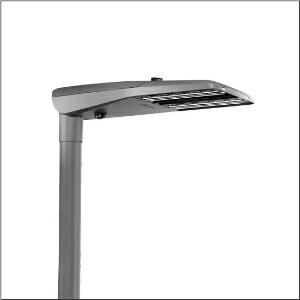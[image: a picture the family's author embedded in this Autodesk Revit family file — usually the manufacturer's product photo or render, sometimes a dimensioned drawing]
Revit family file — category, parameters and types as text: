
# Revit family: streetlight_sl_11_iq_midi___st0_5st0_5_5xc3h51y08me_12eb
name_source: partatom
category: Lighting Fixtures
units: mm (PartAtom-declared; Revit-internal decimal feet)

## family parameters
Cut with Voids When Loaded = No
Host = Face
Light Source = No
Part Type = Normal
Room Calculation Point = No
Round Connector Dimension = Use Diameter
Shared = No

## types (1)
- --- (1 x LED, 17940 lm, 122.7 W, 3000K)
    Apparent Load = 123 VA
    CIE Flux Codes = 43 74 97 100 100
    Color Rendering = 70
    Color Temperature = 3000K
    Default Elevation = 1800 mm
    Description = Streetlight SL 11 iQ midi, mast luminaire, primary light control with 3 zone facetted reflector, of plastic, silver coated, highly specular, primary optical cover: cover, of PMMA, transparent, light distribution: ST0.5ST0.5, light emission: direct distribution, primary light characteristic: asymmetric, installation type: post-top, side-entry, LED, High Power LED, rated luminous flux: 17.940lm, luminous efficacy: 146lm/W, light colour: 730, colour temperature: 3000K, control: presetting dimming logarithmic, Street-Remote, Auto-Match, Temp-Guard, Lumen-Switch, Night-Set, Smart-Wire, Light-Fading, Desk-Remote (wireless, voltage-free reading and setting of iQ features in the workshop via application-optimized NFC function/RFID function), optimised constant luminous flux control (CLO 2.0), with cable H07RN-F 5x 1.5mm², mains connection: 230..240V, AC, 50/60Hz, connection cable pre-assembled, cable length: 12,5m, start of lifetime: 123W, end of service life: 130W, reduction: 56W, luminaire housing, of diecast aluminium, powder-coated, Siteco® metallic grey (DB 702S), please order mast flange separately, inclination adjustable without tools: 0°, 5°, 10°, 15° (post-top) | 0°, -5°, -10°, -15° (side-entry), sealing non-destructively replaceable, multi-level sealing system, length: 780mm, width: 376mm, height: 118mm, mast flange for spigot size: 42mm (side-entry): 5XC10008XM4, 60/48mm (side-entry/post-top): 5XC10108XM2, 76/60mm (side-entry/post-top): 5XC10108XM1, equipment: Power, Smart Interface below and above, protection rating (complete): IP66, insulation class (complete): insulation class II (safety insulation), certification: CE, ENEC, VDE, UKCA, impact resistance: IK09, permissible operating ambient temperature for outdoor applications: -25..+50°C, standard-compliant lighting for roads and squares, Environmental Product Declaration (EPD) tested and certified by an independent institute, packaging unit: 1 piece

Light Distribution: ST0.5ST0.5
    Height = 118 mm
    Lamp = 1 x LED
    Lamp Light Flux = 17940 lm
    Lamp Power = 122.7 W
    Lamp count = 1
    Length = 780 mm
    Luminous efficacy = 146 lm/W
    Manufacturer = Siteco
    ModVariant = No
    Model = 5XC3H51Y08ME
    Number of Poles = 1
    OnlyDefault = Yes
    Power Factor = 1
    Product Name = Streetlight SL 11 iQ midi | ST0.5ST0.5
    Product group = mast luminaire | pylon top
    ProductGroupID = 6100
    Protection Class = Protection class II
    Protection Degree = IP 66
    RLX_Detail_Level = 1
    RLX_Emergency_Light_Flux = 0 lm
    RLX_Emergency_Type = 0
    RLX_Emergency_Type_DB = No
    RlxData = <blob elided: 74349 chars, md5=5a74476a>
    Socket = socket
    Standby Power = 0 W
    System Light Flux = 17940 lm
    System Power = 123 W
    Type Comments = factory setting: luminous flux: 100 % | dim-lin: 254 | 553 mA
    Type Image = l_1004429.jpg
    URL = http://relux.com
    VarID = @adj_064143
    Voltage = 0 V
    Weight = 0.00 kg
    Width = 376 mm

## geometry (parser evidence)
native form markers: Blend x4, Sweep x12
no freeform markers — native parametric forms only
